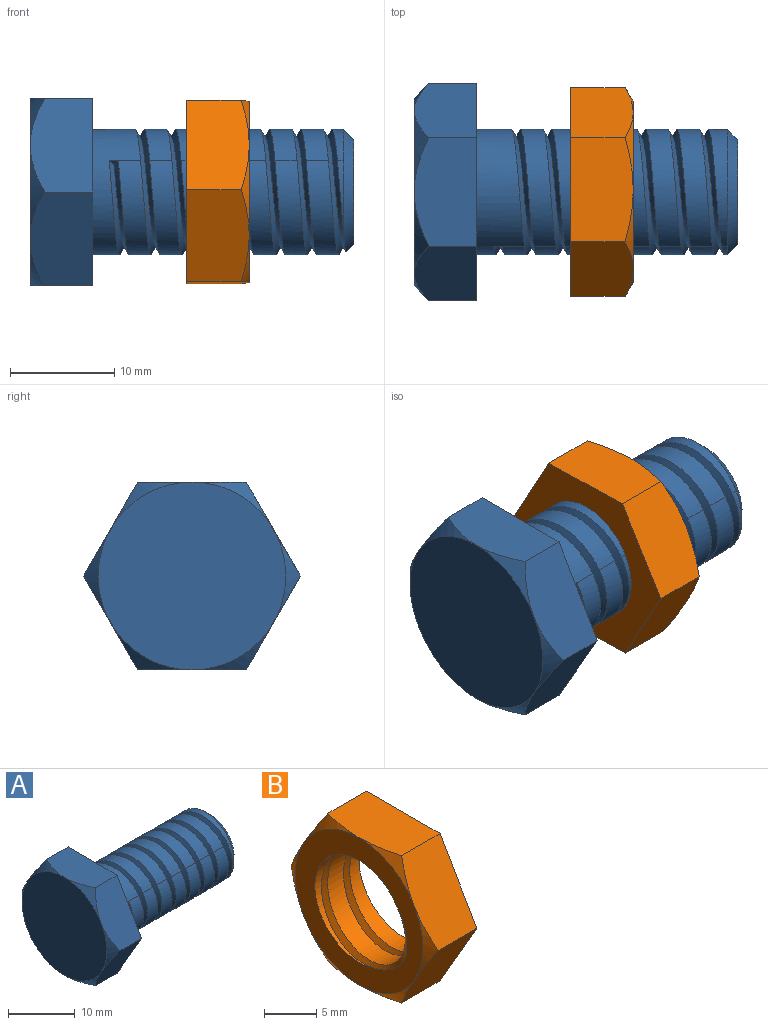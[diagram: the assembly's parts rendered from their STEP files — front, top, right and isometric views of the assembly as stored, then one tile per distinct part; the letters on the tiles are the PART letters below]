
ASSEMBLY  parts=2 mates=1
PART A: 28 faces, bbox 32.2x21.8x21.8 mm
  f0: plane 10.01x7.02mm, normal (0,-0.87,-0.5), area 57.4mm2, adj f1,f5,f16,f18,f22
  f1: plane 10.01x7.02mm, normal (0,-0.87,0.5), area 57.4mm2, adj f0,f2,f16,f21,f22
  f2: plane 11.42x7.02mm, normal (0,0,1), area 57.4mm2, adj f1,f3,f16,f20,f21
  f3: plane 10.01x7.02mm, normal (0,0.87,0.5), area 57.4mm2, adj f2,f4,f16,f19,f20
  f4: plane 10.01x7.02mm, normal (0,0.87,-0.5), area 57.4mm2, adj f3,f5,f16,f17,f19
  f5: plane 11.42x7.02mm, normal (0,0,-1), area 57.4mm2, adj f0,f4,f16,f17,f18
  f6: cylinder r=6mm len=12mm, axis (-1,0,0), area 115.7mm2, adj f7,f16,f25,f27
  f7: cylinder r=6mm len=12mm, axis (-1,0,0), area 80.1mm2, adj f6,f8,f26,f27
  f8: cylinder r=6mm len=12mm, axis (-1,0,0), area 80.2mm2, adj f7,f9,f26,f27
  f9: cylinder r=6mm len=12mm, axis (-1,0,0), area 80.2mm2, adj f8,f10,f26,f27
  f10: cylinder r=6mm len=12mm, axis (-1,0,0), area 80.1mm2, adj f9,f11,f26,f27
  f11: cylinder r=6mm len=12mm, axis (-1,0,0), area 80.1mm2, adj f10,f12,f26,f27
  f12: cylinder r=6mm len=12mm, axis (-1,0,0), area 80.2mm2, adj f11,f13,f26,f27
  f13: cylinder r=6mm len=12mm, axis (-1,0,0), area 64.7mm2, adj f12,f14,f24,f26,f27
  f14: cylinder r=6mm len=6.64mm, axis (-1,0,0), area 2mm2, adj f13,f24,f26
  f15: plane 10x10mm, normal (1,0,0), area 78.5mm2, adj f24
  f16: plane 20.78x18mm, normal (1,0,0), area 167.5mm2, adj f0,f1,f2,f3,f4,f5,f6
  f17: cone r=9mm half-angle=45deg, axis (1,0,0), area 9.8mm2, adj f4,f5,f23
  f18: cone r=9mm half-angle=45deg, axis (1,0,0), area 9.8mm2, adj f0,f5,f23
  f19: cone r=9mm half-angle=45deg, axis (1,0,0), area 9.8mm2, adj f3,f4,f23
  f20: cone r=9mm half-angle=45deg, axis (1,0,0), area 9.8mm2, adj f2,f3,f23
  f21: cone r=9mm half-angle=45deg, axis (1,0,0), area 9.8mm2, adj f1,f2,f23
  f22: cone r=9mm half-angle=45deg, axis (1,0,0), area 9.8mm2, adj f0,f1,f23
  f23: plane 18x18mm, normal (-1,0,0), area 254.5mm2, adj f17,f18,f19,f20,f21,f22
  f24: cone r=5mm half-angle=45deg, axis (-1,0,0), area 43.3mm2, adj f13,f14,f15,f26,f27
  f25: plane 0.87x0.66mm, normal (0,-0.5,-0.87), area 0.3mm2, adj f6,f26,f27
  f26: bspline ~23.19x12mm, area 228.8mm2, adj f7,f8,f9,f10,f11,f12,f13,f14
  f27: bspline ~23.19x12mm, area 233mm2, adj f6,f7,f8,f9,f10,f11,f12,f13
PART B: 18 faces, bbox 7.3x20.8x20.8 mm
  f0: cylinder r=6mm len=12mm, axis (-1,0,0), area 167mm2, adj f1,f8,f15,f16,f17
  f1: plane 17.54x17.54mm, normal (-1,0,0), area 118.5mm2, adj f0,f9,f10,f11,f12,f13,f14,f15
  f2: plane 9.48x6.83mm, normal (0,-0.87,0.5), area 57.3mm2, adj f3,f7,f8,f9,f14
  f3: plane 9.48x6.83mm, normal (0,-0.87,-0.5), area 57.3mm2, adj f2,f4,f8,f13,f14
  f4: plane 10.83x6.83mm, normal (0,0,-1), area 57.3mm2, adj f3,f5,f8,f12,f13
  f5: plane 9.48x6.83mm, normal (0,0.87,-0.5), area 57.3mm2, adj f4,f6,f8,f11,f12
  f6: plane 9.48x6.83mm, normal (0,0.87,0.5), area 57.3mm2, adj f5,f7,f8,f10,f11
  f7: plane 10.83x6.83mm, normal (0,0,1), area 57.3mm2, adj f2,f6,f8,f9,f10
  f8: plane 20x17.32mm, normal (1,0,0), area 146.7mm2, adj f0,f2,f3,f4,f5,f6,f7
  f9: cone r=8.66mm half-angle=60deg, axis (1,0,0), area 7.4mm2, adj f1,f2,f7
  f10: cone r=8.66mm half-angle=60deg, axis (1,0,0), area 7.4mm2, adj f1,f6,f7
  f11: cone r=8.66mm half-angle=60deg, axis (1,0,0), area 7.4mm2, adj f1,f5,f6
  f12: cone r=8.66mm half-angle=60deg, axis (1,0,0), area 7.4mm2, adj f1,f4,f5
  f13: cone r=8.66mm half-angle=60deg, axis (1,0,0), area 7.4mm2, adj f1,f3,f4
  f14: cone r=8.66mm half-angle=60deg, axis (1,0,0), area 7.4mm2, adj f1,f2,f3
  f15: bspline ~13.45x13.44mm, area 60.6mm2, adj f0,f1,f16,f17
  f16: bspline ~15.54x13.5mm, area 65.2mm2, adj f0,f1,f15,f17
  f17: plane 0.84x0.65mm, normal (-0.08,0.5,0.86), area 0.3mm2, adj f0,f15,f16
PLACE A t=(0,20.27,0)mm fixed
PLACE B rot(axis=(0,0.87,0.49),180deg) t=(14.99,20.27,0)mm
MATE cylindrical A.f6 <-> B.f0  axis (1,0,0) through (25,20.27,0)mm
